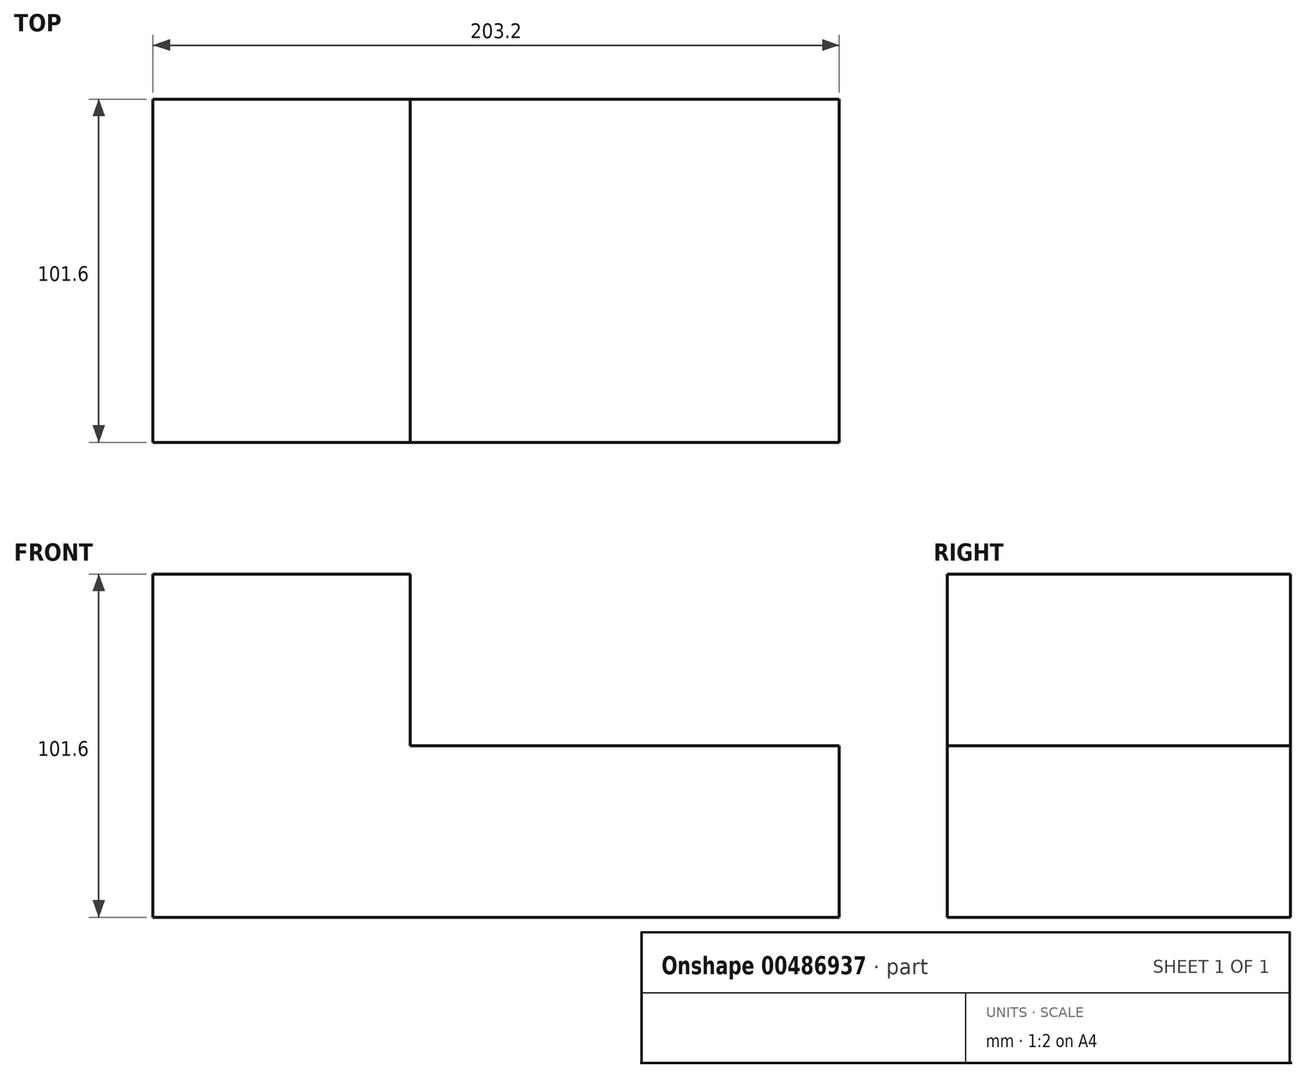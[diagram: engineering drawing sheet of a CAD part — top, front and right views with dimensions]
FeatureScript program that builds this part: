
annotation { "Feature Type Name" : "Feature", "Feature Type Description" : "" }
export const myFeature = defineFeature(function(context is Context, id is Id, definition is map)
    precondition{}
    {
        {
            var Q0;
            Q0=qCreatedBy(makeId("Front.planeOp"),FACE);
            var sketch = newSketch(context, id + "F0", { "sketchPlane" : qUnion([Q0])});
            skLineSegment(sketch, "E0.bottom", {"start": v(0, 0) * mm, "end": v(203.2, 0) * mm});
            skLineSegment(sketch, "E0.top", {"start": v(0, 101.6) * mm, "end": v(76.2, 101.6) * mm});
            skLineSegment(sketch, "E0.left", {"start": v(0, 0) * mm, "end": v(0, 101.6) * mm});
            skLineSegment(sketch, "E0.right", {"start": v(203.2, 0) * mm, "end": v(203.2, 50.8) * mm});
            skLineSegment(sketch, "E1", {"start": v(203.2, 50.8) * mm, "end": v(76.2, 50.8) * mm});
            skLineSegment(sketch, "E2", {"start": v(76.2, 50.8) * mm, "end": v(76.2, 101.6) * mm});
            skSolve(sketch);
        }
        {
            var Q0;
            Q0 = qSketchRegion(id + "F0", true);
            extrude(context, id + "F1", {"entities" : qUnion([Q0]), "depth" : 101.6 * mm});
        }
    });
